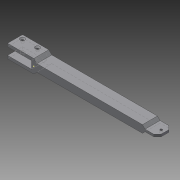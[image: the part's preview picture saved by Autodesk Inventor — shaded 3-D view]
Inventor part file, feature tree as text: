
AUTODESK INVENTOR PART (.ipt)
format: ipt  version: 2015 (Build 190159000, 159)  size: 228,864 bytes
history: native  units: mm
features: sketch x12, extrude x9, chamfer x4, hole x2
ambient origin geometry x8: Origin, YZ Plane, XZ Plane, XY Plane, X Axis, Y Axis, Z Axis, Center Point
bodies: Solid1 (feature_tree)
feature tree (27):
  extrude  "Extrusion1"  Depth=20.0mm
  sketch  "Sketch2"  dims[d2=10.0mm d3=0.0mm d4=4.0mm]
  extrude  "Extrusion2"  Depth=4.0mm
  extrude  "Extrusion3"  Depth=4.0mm TaperAngle=0.0deg
  hole  "Hole1"  [1 undecoded]
  chamfer  "Chamfer1"  Distance=4.0mm Angle=45.0deg
  extrude  "Extrusion4"  Depth=4.0mm
  extrude  "Extrusion5"  Depth=20.0mm TaperAngle=0.0deg
  chamfer  "Chamfer2"  Distance=4.0mm
  extrude  "Extrusion6"  Depth=4.0mm
  extrude  "Extrusion7"  Depth=20.0mm TaperAngle=0.0deg
  extrude  "Extrusion8"  Depth=4.0mm TaperAngle=45.0deg
  extrude  "Extrusion9"  Depth=3.5mm
  hole  "Hole2"  [1 undecoded]
  chamfer  "Chamfer3"  Distance=5.0mm
  chamfer  "Chamfer4"  Distance=5.0mm
  sketch  "Sketch1"  dims[d0=150.0mm d1=20.0mm]
  sketch  "Sketch3"  dims[d5=4.0mm d6=5.0mm d7=0.0mm]
  sketch  "Sketch4"  dims[d8=30.0mm d9=0.0mm d10=5.0mm]
  sketch  "Sketch5"  dims[d11=5.0mm]
  sketch  "Sketch6"  dims[d12=5.0mm]
  sketch  "Sketch7"  dims[d13=5.0mm]
  sketch  "Sketch8"  dims[d14=3.0mm d15=6.0mm d16=6.0mm d17=2.0mm d18=90.0deg d19=30.0mm d20=20.594885mm d21=4.0mm d22=2.0mm d23=45.0deg]
  sketch  "Sketch9"  dims[d24=4.0mm d25=4.0mm]
  sketch  "Sketch10"  dims[d26=5.0mm d27=20.0mm d28=0.0mm]
  sketch  "Sketch11"  dims[d29=30.0mm]
  sketch  "Sketch12"  dims[d30=30.0mm d31=4.0mm d32=4.0mm d33=20.0mm d34=0.0mm d35=4.0mm d36=2.0mm d37=45.0deg d38=5.0mm d39=5.0mm d40=5.0mm d41=5.0mm d42=5.0mm d43=5.0mm d44=5.0mm d45=5.0mm d46=4.0mm d47=4.0mm d48=4.0mm d49=4.0mm d50=20.0mm d51=0.0mm d52=1.851607mm d53=20.0mm d54=0.0mm d55=20.0mm d56=0.0mm d57=3.0mm d58=3.5mm d59=20.0mm d60=20.0mm d61=0.0mm d62=10.0mm d63=5.0mm d64=3.0mm d65=6.0mm d66=4.0mm d67=2.0mm d68=90.0deg d69=8.0mm d70=20.594885mm d71=5.0mm d72=2.0mm d73=45.0deg d74=3.5mm d75=2.0mm d76=45.0deg]
note: 2 required parameter values undecoded (feature->parameter linkage not recoverable at this tier; creation-order binding heuristic only, values carry confidence <= 0.55)
